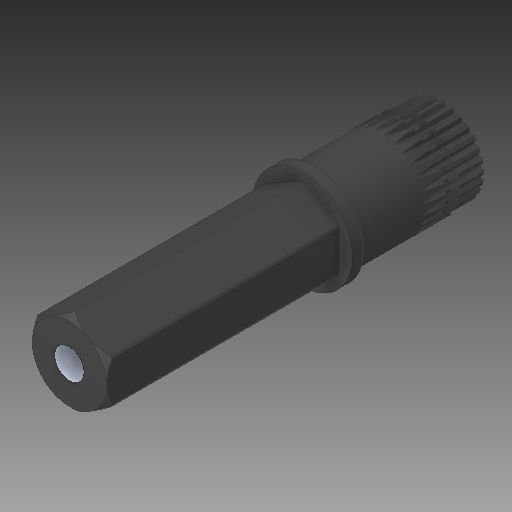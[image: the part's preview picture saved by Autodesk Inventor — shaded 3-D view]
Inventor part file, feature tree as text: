
AUTODESK INVENTOR PART (.ipt)
format: ipt  version: 2017 (Build 210142000, 142)  size: 1,435,648 bytes
history: native  units: in
note: dims shown in document units (in); Inventor stores cm internally (conversion verified against a paired STEP export)
features: fillet x1
ambient origin geometry x8: Origin, YZ Plane, XZ Plane, XY Plane, X Axis, Y Axis, Z Axis, Center Point
bodies: Solid1 (feature_tree)
feature tree (1):
  fillet  "Fillet5"  [1 undecoded]
note: 1 required parameter value undecoded (feature->parameter linkage not recoverable at this tier; creation-order binding heuristic only, values carry confidence <= 0.55)
